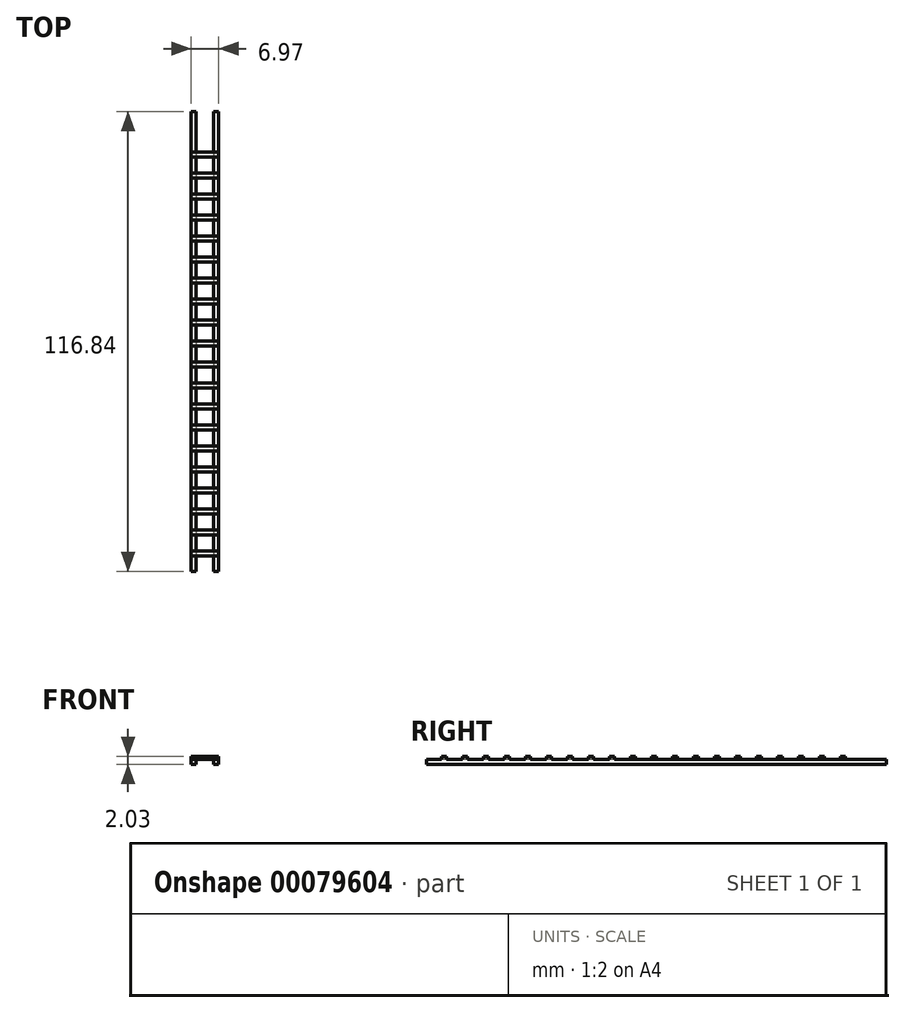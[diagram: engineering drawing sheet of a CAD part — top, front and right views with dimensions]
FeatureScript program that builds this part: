
annotation { "Feature Type Name" : "Feature", "Feature Type Description" : "" }
export const myFeature = defineFeature(function(context is Context, id is Id, definition is map)
    precondition{}
    {
        {
            var Q0;
            Q0=qCreatedBy(makeId("Top.planeOp"),FACE);
            var sketch = newSketch(context, id + "F0", { "sketchPlane" : qUnion([Q0])});
            skLineSegment(sketch, "E0.bottom", {"start": v(-3.47, 88.08) * mm, "end": v(-2.2, 88.08) * mm});
            skLineSegment(sketch, "E0.top", {"start": v(-3.47, -28.76) * mm, "end": v(-2.2, -28.76) * mm});
            skLineSegment(sketch, "E0.left", {"start": v(-3.47, 88.08) * mm, "end": v(-3.47, -28.76) * mm});
            skLineSegment(sketch, "E0.right", {"start": v(-2.2, 88.08) * mm, "end": v(-2.2, -28.76) * mm});
            skLineSegment(sketch, "E1.MirrorCS", {"start": v(3.47, 88.08) * mm, "end": v(2.2, 88.08) * mm});
            skLineSegment(sketch, "E2.MirrorCS", {"start": v(3.47, -28.76) * mm, "end": v(2.2, -28.76) * mm});
            skLineSegment(sketch, "E3.MirrorCS", {"start": v(2.2, 88.08) * mm, "end": v(2.2, -28.76) * mm});
            skLineSegment(sketch, "E4.MirrorCS", {"start": v(3.47, 88.08) * mm, "end": v(3.47, -28.76) * mm});
            skSolve(sketch);
        }
        {
            var Q0;
            Q0 = qSketchRegion(id + "F0", true);
            extrude(context, id + "F1", {"entities" : qUnion([Q0]), "depth" : 1.27 * mm});
        }
        {
            var Q0;
            Q0=makeQuery(id+"F1.opExtrude","CAP_FACE",FACE,{"disambiguationData":[OSD([sQuery(id+"F0.wireOp",EDGE,"E0.bottom"),sQuery(id+"F0.wireOp",EDGE,"E0.top"),sQuery(id+"F0.wireOp",EDGE,"E0.left"),sQuery(id+"F0.wireOp",EDGE,"E0.right")])],"isStart":false});
            var sketch = newSketch(context, id + "F2", { "sketchPlane" : qUnion([Q0])});
            skLineSegment(sketch, "E5.bottom", {"start": v(-3.47, -23.6) * mm, "end": v(3.47, -23.6) * mm});
            skLineSegment(sketch, "E5.top", {"start": v(-3.47, -24.88) * mm, "end": v(3.47, -24.88) * mm});
            skLineSegment(sketch, "E5.left", {"start": v(-3.47, -23.6) * mm, "end": v(-3.47, -24.88) * mm});
            skLineSegment(sketch, "E5.right", {"start": v(3.47, -23.6) * mm, "end": v(3.47, -24.88) * mm});
            skLineSegment(sketch, "E6.1.0.0", {"start": v(-3.47, -19.54) * mm, "end": v(3.48, -19.54) * mm});
            skLineSegment(sketch, "E6.1.0.1", {"start": v(-3.47, -18.27) * mm, "end": v(3.48, -18.27) * mm});
            skLineSegment(sketch, "E6.1.0.2", {"start": v(3.48, -18.27) * mm, "end": v(3.48, -19.54) * mm});
            skLineSegment(sketch, "E6.1.0.3", {"start": v(-3.47, -18.27) * mm, "end": v(-3.47, -19.54) * mm});
            skLineSegment(sketch, "E6.2.0.0", {"start": v(-3.47, -14.2) * mm, "end": v(3.48, -14.2) * mm});
            skLineSegment(sketch, "E6.2.0.1", {"start": v(-3.47, -12.94) * mm, "end": v(3.48, -12.94) * mm});
            skLineSegment(sketch, "E6.2.0.2", {"start": v(3.48, -12.94) * mm, "end": v(3.48, -14.2) * mm});
            skLineSegment(sketch, "E6.2.0.3", {"start": v(-3.47, -12.94) * mm, "end": v(-3.47, -14.2) * mm});
            skLineSegment(sketch, "E6.3.0.0", {"start": v(-3.47, -8.88) * mm, "end": v(3.48, -8.88) * mm});
            skLineSegment(sketch, "E6.3.0.1", {"start": v(-3.47, -7.6) * mm, "end": v(3.48, -7.6) * mm});
            skLineSegment(sketch, "E6.3.0.2", {"start": v(3.48, -7.6) * mm, "end": v(3.48, -8.88) * mm});
            skLineSegment(sketch, "E6.3.0.3", {"start": v(-3.47, -7.6) * mm, "end": v(-3.47, -8.88) * mm});
            skLineSegment(sketch, "E6.4.0.0", {"start": v(-3.47, -3.54) * mm, "end": v(3.48, -3.54) * mm});
            skLineSegment(sketch, "E6.4.0.1", {"start": v(-3.47, -2.27) * mm, "end": v(3.48, -2.27) * mm});
            skLineSegment(sketch, "E6.4.0.2", {"start": v(3.48, -2.27) * mm, "end": v(3.48, -3.54) * mm});
            skLineSegment(sketch, "E6.4.0.3", {"start": v(-3.47, -2.27) * mm, "end": v(-3.47, -3.54) * mm});
            skLineSegment(sketch, "E6.5.0.0", {"start": v(-3.47, 1.8) * mm, "end": v(3.48, 1.8) * mm});
            skLineSegment(sketch, "E6.5.0.1", {"start": v(-3.47, 3.06) * mm, "end": v(3.48, 3.06) * mm});
            skLineSegment(sketch, "E6.5.0.2", {"start": v(3.48, 3.06) * mm, "end": v(3.48, 1.8) * mm});
            skLineSegment(sketch, "E6.5.0.3", {"start": v(-3.47, 3.06) * mm, "end": v(-3.47, 1.8) * mm});
            skLineSegment(sketch, "E6.6.0.0", {"start": v(-3.47, 7.13) * mm, "end": v(3.48, 7.13) * mm});
            skLineSegment(sketch, "E6.6.0.1", {"start": v(-3.47, 8.4) * mm, "end": v(3.48, 8.4) * mm});
            skLineSegment(sketch, "E6.6.0.2", {"start": v(3.48, 8.4) * mm, "end": v(3.48, 7.13) * mm});
            skLineSegment(sketch, "E6.6.0.3", {"start": v(-3.47, 8.4) * mm, "end": v(-3.47, 7.13) * mm});
            skLineSegment(sketch, "E6.7.0.0", {"start": v(-3.47, 12.46) * mm, "end": v(3.48, 12.46) * mm});
            skLineSegment(sketch, "E6.7.0.1", {"start": v(-3.47, 13.73) * mm, "end": v(3.48, 13.73) * mm});
            skLineSegment(sketch, "E6.7.0.2", {"start": v(3.48, 13.73) * mm, "end": v(3.48, 12.46) * mm});
            skLineSegment(sketch, "E6.7.0.3", {"start": v(-3.47, 13.73) * mm, "end": v(-3.47, 12.46) * mm});
            skLineSegment(sketch, "E6.8.0.0", {"start": v(-3.47, 17.8) * mm, "end": v(3.48, 17.8) * mm});
            skLineSegment(sketch, "E6.8.0.1", {"start": v(-3.47, 19.06) * mm, "end": v(3.48, 19.06) * mm});
            skLineSegment(sketch, "E6.8.0.2", {"start": v(3.48, 19.06) * mm, "end": v(3.48, 17.8) * mm});
            skLineSegment(sketch, "E6.8.0.3", {"start": v(-3.47, 19.06) * mm, "end": v(-3.47, 17.8) * mm});
            skLineSegment(sketch, "E6.9.0.0", {"start": v(-3.46, 23.13) * mm, "end": v(3.49, 23.13) * mm});
            skLineSegment(sketch, "E6.9.0.1", {"start": v(-3.46, 24.4) * mm, "end": v(3.49, 24.4) * mm});
            skLineSegment(sketch, "E6.9.0.2", {"start": v(3.49, 24.4) * mm, "end": v(3.49, 23.13) * mm});
            skLineSegment(sketch, "E6.9.0.3", {"start": v(-3.46, 24.4) * mm, "end": v(-3.46, 23.13) * mm});
            skLineSegment(sketch, "E6.10.0.0", {"start": v(-3.46, 28.46) * mm, "end": v(3.49, 28.46) * mm});
            skLineSegment(sketch, "E6.10.0.1", {"start": v(-3.46, 29.73) * mm, "end": v(3.49, 29.73) * mm});
            skLineSegment(sketch, "E6.10.0.2", {"start": v(3.49, 29.73) * mm, "end": v(3.49, 28.46) * mm});
            skLineSegment(sketch, "E6.10.0.3", {"start": v(-3.46, 29.73) * mm, "end": v(-3.46, 28.46) * mm});
            skLineSegment(sketch, "E6.11.0.0", {"start": v(-3.46, 33.8) * mm, "end": v(3.49, 33.8) * mm});
            skLineSegment(sketch, "E6.11.0.1", {"start": v(-3.46, 35.07) * mm, "end": v(3.49, 35.07) * mm});
            skLineSegment(sketch, "E6.11.0.2", {"start": v(3.49, 35.07) * mm, "end": v(3.49, 33.8) * mm});
            skLineSegment(sketch, "E6.11.0.3", {"start": v(-3.46, 35.07) * mm, "end": v(-3.46, 33.8) * mm});
            skLineSegment(sketch, "E6.12.0.0", {"start": v(-3.46, 39.13) * mm, "end": v(3.49, 39.13) * mm});
            skLineSegment(sketch, "E6.12.0.1", {"start": v(-3.46, 40.4) * mm, "end": v(3.49, 40.4) * mm});
            skLineSegment(sketch, "E6.12.0.2", {"start": v(3.49, 40.4) * mm, "end": v(3.49, 39.13) * mm});
            skLineSegment(sketch, "E6.12.0.3", {"start": v(-3.46, 40.4) * mm, "end": v(-3.46, 39.13) * mm});
            skLineSegment(sketch, "E6.13.0.0", {"start": v(-3.46, 44.46) * mm, "end": v(3.5, 44.46) * mm});
            skLineSegment(sketch, "E6.13.0.1", {"start": v(-3.46, 45.73) * mm, "end": v(3.5, 45.73) * mm});
            skLineSegment(sketch, "E6.13.0.2", {"start": v(3.5, 45.73) * mm, "end": v(3.5, 44.46) * mm});
            skLineSegment(sketch, "E6.13.0.3", {"start": v(-3.46, 45.73) * mm, "end": v(-3.46, 44.46) * mm});
            skLineSegment(sketch, "E6.14.0.0", {"start": v(-3.46, 49.8) * mm, "end": v(3.5, 49.8) * mm});
            skLineSegment(sketch, "E6.14.0.1", {"start": v(-3.46, 51.07) * mm, "end": v(3.5, 51.07) * mm});
            skLineSegment(sketch, "E6.14.0.2", {"start": v(3.5, 51.07) * mm, "end": v(3.5, 49.8) * mm});
            skLineSegment(sketch, "E6.14.0.3", {"start": v(-3.46, 51.07) * mm, "end": v(-3.46, 49.8) * mm});
            skLineSegment(sketch, "E6.15.0.0", {"start": v(-3.46, 55.13) * mm, "end": v(3.5, 55.13) * mm});
            skLineSegment(sketch, "E6.15.0.1", {"start": v(-3.46, 56.4) * mm, "end": v(3.5, 56.4) * mm});
            skLineSegment(sketch, "E6.15.0.2", {"start": v(3.5, 56.4) * mm, "end": v(3.5, 55.13) * mm});
            skLineSegment(sketch, "E6.15.0.3", {"start": v(-3.46, 56.4) * mm, "end": v(-3.46, 55.13) * mm});
            skLineSegment(sketch, "E6.16.0.0", {"start": v(-3.46, 60.47) * mm, "end": v(3.5, 60.47) * mm});
            skLineSegment(sketch, "E6.16.0.1", {"start": v(-3.46, 61.74) * mm, "end": v(3.5, 61.74) * mm});
            skLineSegment(sketch, "E6.16.0.2", {"start": v(3.5, 61.74) * mm, "end": v(3.5, 60.47) * mm});
            skLineSegment(sketch, "E6.16.0.3", {"start": v(-3.46, 61.74) * mm, "end": v(-3.46, 60.47) * mm});
            skLineSegment(sketch, "E6.17.0.0", {"start": v(-3.45, 65.8) * mm, "end": v(3.5, 65.8) * mm});
            skLineSegment(sketch, "E6.17.0.1", {"start": v(-3.45, 67.07) * mm, "end": v(3.5, 67.07) * mm});
            skLineSegment(sketch, "E6.17.0.2", {"start": v(3.5, 67.07) * mm, "end": v(3.5, 65.8) * mm});
            skLineSegment(sketch, "E6.17.0.3", {"start": v(-3.45, 67.07) * mm, "end": v(-3.45, 65.8) * mm});
            skLineSegment(sketch, "E6.18.0.0", {"start": v(-3.45, 71.13) * mm, "end": v(3.5, 71.13) * mm});
            skLineSegment(sketch, "E6.18.0.1", {"start": v(-3.45, 72.4) * mm, "end": v(3.5, 72.4) * mm});
            skLineSegment(sketch, "E6.18.0.2", {"start": v(3.5, 72.4) * mm, "end": v(3.5, 71.13) * mm});
            skLineSegment(sketch, "E6.18.0.3", {"start": v(-3.45, 72.4) * mm, "end": v(-3.45, 71.13) * mm});
            skLineSegment(sketch, "E6.direction1", {"start": v(-3.47, -24.88) * mm, "end": v(-3.47, -19.54) * mm, "construction": true});
            skLineSegment(sketch, "E7.0.19.0", {"start": v(-3.45, 76.47) * mm, "end": v(3.5, 76.47) * mm});
            skLineSegment(sketch, "E7.3.19.0", {"start": v(-3.45, 77.74) * mm, "end": v(3.5, 77.74) * mm});
            skLineSegment(sketch, "E7.6.19.0", {"start": v(3.5, 77.74) * mm, "end": v(3.5, 76.47) * mm});
            skLineSegment(sketch, "E7.9.19.0", {"start": v(-3.45, 77.74) * mm, "end": v(-3.45, 76.47) * mm});
            skSolve(sketch);
        }
        {
            var Q0;
            Q0 = qSketchRegion(id + "F2", true);
            extrude(context, id + "F3", {"entities" : qUnion([Q0]), "operationType" : NewBodyOperationType.ADD, "depth" : 0.76 * mm});
        }
    });
